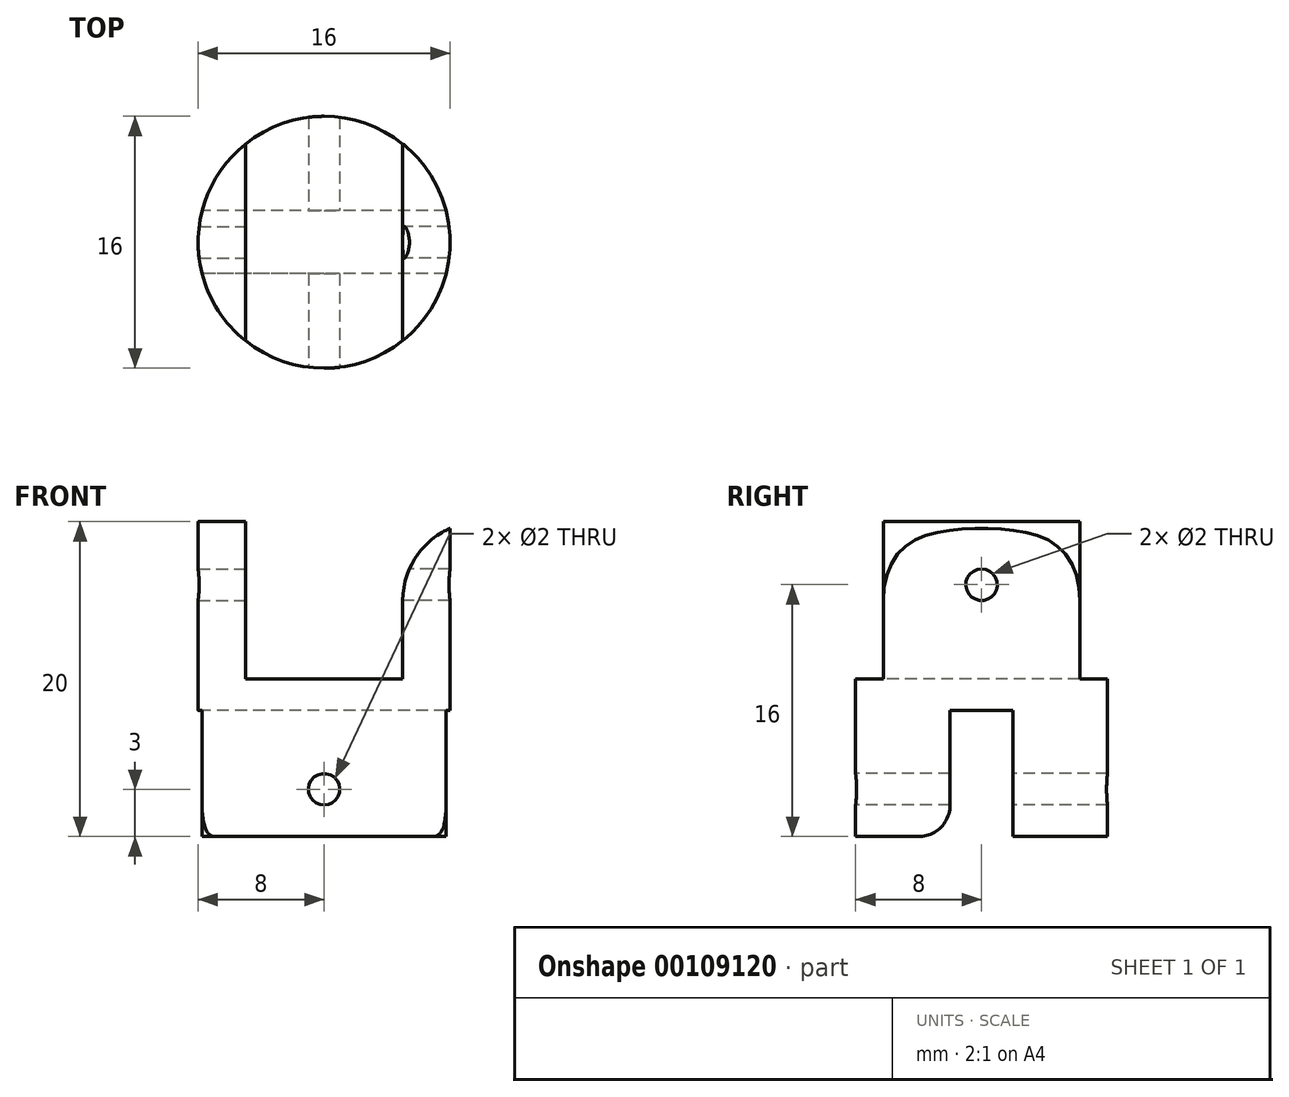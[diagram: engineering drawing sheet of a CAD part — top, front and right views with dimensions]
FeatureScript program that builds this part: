
annotation { "Feature Type Name" : "Feature", "Feature Type Description" : "" }
export const myFeature = defineFeature(function(context is Context, id is Id, definition is map)
    precondition{}
    {
        {
            var Q0;
            Q0=qCreatedBy(makeId("Top.planeOp"),FACE);
            var sketch = newSketch(context, id + "F0", { "sketchPlane" : qUnion([Q0])});
            skCircle(sketch, "E0", {"center": v(0, 0) * mm, "radius": 8 * mm});
            skSolve(sketch);
        }
        {
            var Q0;
            Q0 = qSketchRegion(id + "F0", true);
            extrude(context, id + "F1", {"entities" : qUnion([Q0]), "depth" : 20 * mm});
        }
        {
            var Q0;
            Q0=makeQuery(id+"F1.opExtrude","CAP_FACE",FACE,{"disambiguationData":[OSD([sQuery(id+"F0.wireOp",EDGE,"E0")])],"isStart":false});
            var sketch = newSketch(context, id + "F2", { "sketchPlane" : qUnion([Q0])});
            skPoint(sketch, "E1.middle", {"position": v(0, 0) * mm});
            skLineSegment(sketch, "E2.bottom", {"start": v(5, 12) * mm, "end": v(-5, 12) * mm});
            skLineSegment(sketch, "E2.top", {"start": v(5, -12) * mm, "end": v(-5, -12) * mm});
            skLineSegment(sketch, "E2.left", {"start": v(5, 12) * mm, "end": v(5, -12) * mm});
            skLineSegment(sketch, "E2.right", {"start": v(-5, 12) * mm, "end": v(-5, -12) * mm});
            skSolve(sketch);
        }
        {
            var Q0;
            Q0 = qSketchRegion(id + "F2", true);
            extrude(context, id + "F3", {"entities" : qUnion([Q0]), "operationType" : NewBodyOperationType.REMOVE, "oppositeDirection" : true, "depth" : 10 * mm});
        }
        {
            var Q0;
            Q0=makeQuery(id+"F1.opExtrude","CAP_FACE",FACE,{"disambiguationData":[OSD([sQuery(id+"F0.wireOp",EDGE,"E0")])],"isStart":true});
            var sketch = newSketch(context, id + "F4", { "sketchPlane" : qUnion([Q0])});
            skPoint(sketch, "E3.middle", {"position": v(0, 0) * mm});
            skLineSegment(sketch, "E4.bottom", {"start": v(9.5, -2) * mm, "end": v(-9.5, -2) * mm});
            skLineSegment(sketch, "E4.top", {"start": v(9.5, 2) * mm, "end": v(-9.5, 2) * mm});
            skLineSegment(sketch, "E4.left", {"start": v(9.5, -2) * mm, "end": v(9.5, 2) * mm});
            skLineSegment(sketch, "E4.right", {"start": v(-9.5, -2) * mm, "end": v(-9.5, 2) * mm});
            skSolve(sketch);
        }
        {
            var Q0;
            Q0 = qSketchRegion(id + "F4", true);
            extrude(context, id + "F5", {"entities" : qUnion([Q0]), "operationType" : NewBodyOperationType.REMOVE, "oppositeDirection" : true, "depth" : 8 * mm});
        }
        {
            var Q0;
            Q0=makeQuery(id+"F3.boolean.opBoolean","COPY",FACE,{"derivedFrom":makeQuery(id+"F3.opExtrude","SWEPT_FACE",FACE,{"disambiguationData":[OSD([sQuery(id+"F2.wireOp",EDGE,"E2.right")])]})});
            var sketch = newSketch(context, id + "F6", { "sketchPlane" : qUnion([Q0])});
            skCircle(sketch, "E5", {"center": v(0, 16) * mm, "radius": 1 * mm});
            skSolve(sketch);
        }
        {
            var Q0;
            Q0 = qSketchRegion(id + "F6", true);
            extrude(context, id + "F7", {"entities" : qUnion([Q0]), "operationType" : NewBodyOperationType.REMOVE, "oppositeDirection" : true, "depth" : 5 * mm});
        }
        {
            var Q0;
            Q0=makeQuery(id+"F3.boolean.opBoolean","COPY",FACE,{"derivedFrom":makeQuery(id+"F3.opExtrude","SWEPT_FACE",FACE,{"disambiguationData":[OSD([sQuery(id+"F2.wireOp",EDGE,"E2.left")])]})});
            var sketch = newSketch(context, id + "F8", { "sketchPlane" : qUnion([Q0])});
            skCircle(sketch, "E6", {"center": v(0, 16) * mm, "radius": 1 * mm});
            skSolve(sketch);
        }
        {
            var Q0;
            Q0 = qSketchRegion(id + "F8", true);
            extrude(context, id + "F9", {"entities" : qUnion([Q0]), "operationType" : NewBodyOperationType.REMOVE, "oppositeDirection" : true, "depth" : 5 * mm});
        }
        {
            var Q0;
            Q0=qCreatedBy(makeId("Front.planeOp"),FACE);
            var sketch = newSketch(context, id + "F10", { "sketchPlane" : qUnion([Q0])});
            skCircle(sketch, "E7", {"center": v(0, 3) * mm, "radius": 1 * mm});
            skSolve(sketch);
        }
        {
            var Q0;
            Q0 = qSketchRegion(id + "F10", true);
            extrude(context, id + "F11", {"entities" : qUnion([Q0]), "operationType" : NewBodyOperationType.REMOVE, "endBound" : BoundingType.SYMMETRIC, "oppositeDirection" : true, "depth" : 16 * mm});
        }
        {
            var Q0;
            Q0=makeQuery(id+"F3.boolean.opBoolean","COPY",EDGE,{"derivedFrom":makeQuery(id+"F3.opExtrude","CAP_EDGE",EDGE,{"disambiguationData":[OSD([sQuery(id+"F2.wireOp",EDGE,"E2.right")])],"isStart":true})});
            var Q1;
            Q1=makeQuery(id+"F3.boolean.opBoolean","COPY",EDGE,{"derivedFrom":makeQuery(id+"F3.opExtrude","CAP_EDGE",EDGE,{"disambiguationData":[OSD([sQuery(id+"F2.wireOp",EDGE,"E2.left")])],"isStart":true})});
            fillet(context, id + "F12", {"entities" : qUnion([Q0, Q1]), "radius" : 5 * mm, "tangentPropagation" : true, "allowEdgeOverflow" : false});
        }
        {
            var Q0;
            Q0=makeQuery(id+"F5.boolean.opBoolean","COPY",EDGE,{"derivedFrom":makeQuery(id+"F5.opExtrude","CAP_EDGE",EDGE,{"disambiguationData":[OSD([sQuery(id+"F4.wireOp",EDGE,"E4.top")])],"isStart":true})});
            var Q1;
            Q1=makeQuery(id+"F5.boolean.opBoolean","COPY",EDGE,{"derivedFrom":makeQuery(id+"F5.opExtrude","CAP_EDGE",EDGE,{"disambiguationData":[OSD([sQuery(id+"F4.wireOp",EDGE,"E4.bottom")])],"isStart":true})});
            fillet(context, id + "F13", {"entities" : qUnion([Q0, Q1]), "radius" : 2 * mm, "tangentPropagation" : true, "allowEdgeOverflow" : false});
        }
    });
